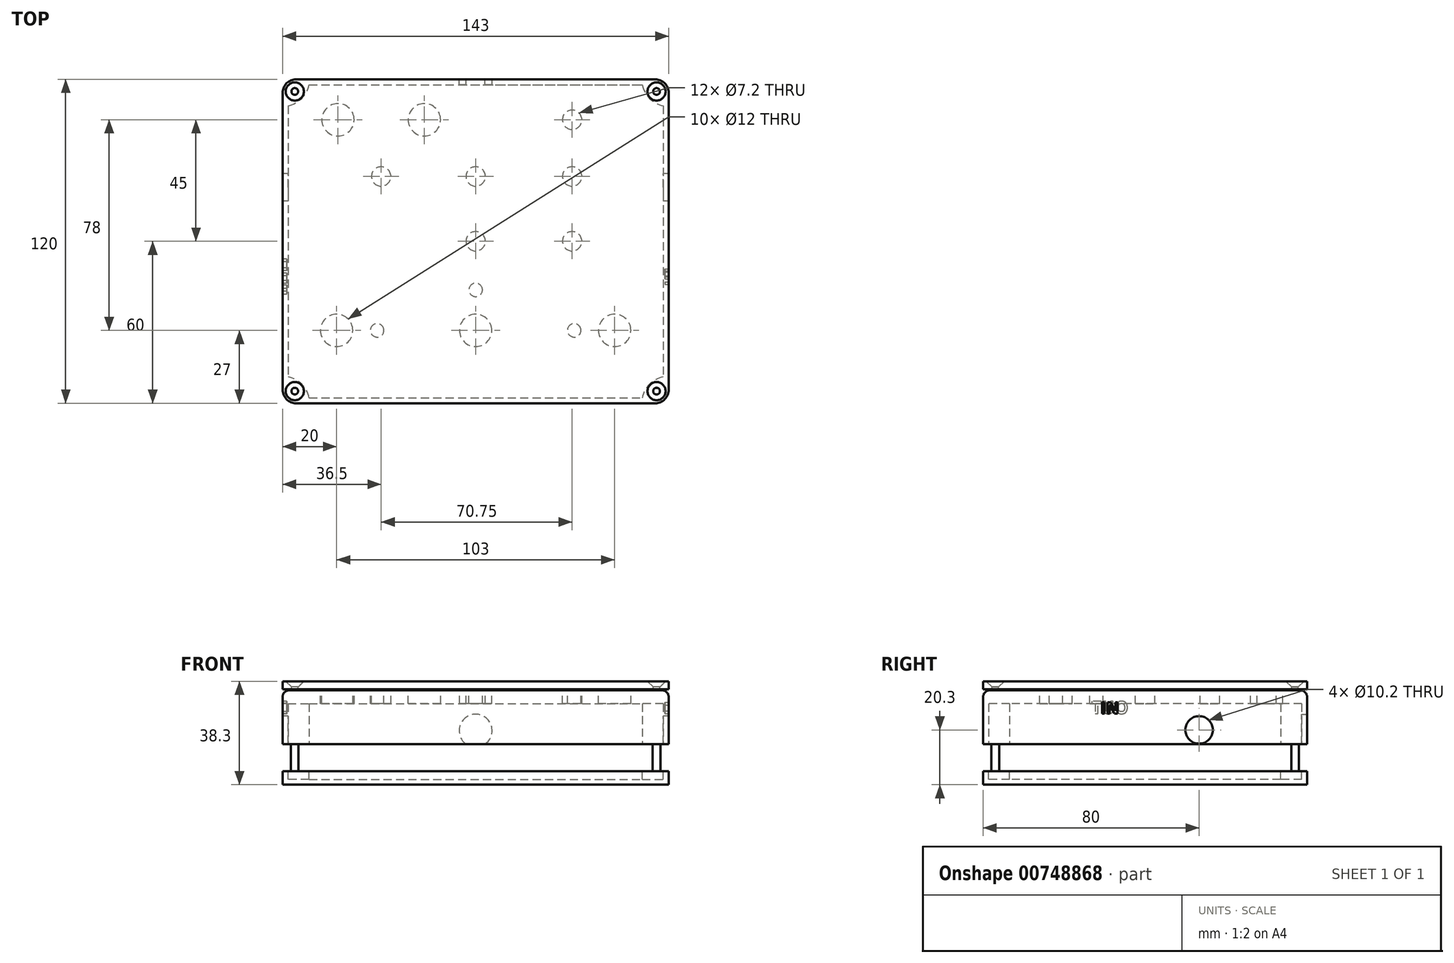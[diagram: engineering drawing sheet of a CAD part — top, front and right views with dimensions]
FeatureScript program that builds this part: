
annotation { "Feature Type Name" : "Feature", "Feature Type Description" : "" }
export const myFeature = defineFeature(function(context is Context, id is Id, definition is map)
    precondition{}
    {
        {
            var Q0;
            Q0=qCreatedBy(makeId("Top.planeOp"),FACE);
            var sketch = newSketch(context, id + "F0", { "sketchPlane" : qUnion([Q0])});
            skCircle(sketch, "E0", {"center": v(-51, 45) * mm, "radius": 6 * mm});
            skCircle(sketch, "E1", {"center": v(-19, 45) * mm, "radius": 6 * mm});
            skCircle(sketch, "E2", {"center": v(-35, 24) * mm, "radius": 3.6 * mm});
            skLineSegment(sketch, "E3", {"start": v(-51, 45) * mm, "end": v(-19, 45) * mm, "construction": true});
            skPoint(sketch, "E4.orphan", {"position": v(-57.53, 45) * mm});
            skLineSegment(sketch, "E5", {"start": v(-35, 15.96) * mm, "end": v(-35, -9.02) * mm, "construction": true});
            skPoint(sketch, "E5.startSnap0", {"position": v(-35, 45) * mm});
            skCircle(sketch, "E6", {"center": v(-51.5, -33) * mm, "radius": 6 * mm});
            skCircle(sketch, "E7", {"center": v(51.5, -33) * mm, "radius": 6 * mm});
            skLineSegment(sketch, "E8.bottom", {"start": v(-71.5, 60) * mm, "end": v(71.5, 60) * mm});
            skLineSegment(sketch, "E8.top", {"start": v(-71.5, -60) * mm, "end": v(71.5, -60) * mm});
            skLineSegment(sketch, "E8.left", {"start": v(-71.5, 60) * mm, "end": v(-71.5, -60) * mm});
            skLineSegment(sketch, "E8.right", {"start": v(71.5, 60) * mm, "end": v(71.5, -60) * mm});
            skPoint(sketch, "E9.center.orphan", {"position": v(0, -43) * mm});
            skCircle(sketch, "E10", {"center": v(0, 24) * mm, "radius": 3.6 * mm});
            skCircle(sketch, "E11", {"center": v(0, 0) * mm, "radius": 3.6 * mm});
            skCircle(sketch, "E12", {"center": v(0, -33) * mm, "radius": 6 * mm});
            skCircle(sketch, "E13", {"center": v(-36.5, -33) * mm, "radius": 2.5 * mm});
            skCircle(sketch, "E14", {"center": v(0, -18) * mm, "radius": 2.5 * mm});
            skCircle(sketch, "E15", {"center": v(36.5, -33) * mm, "radius": 2.5 * mm});
            skLineSegment(sketch, "E16", {"start": v(35.75, 70.32) * mm, "end": v(35.75, 16.59) * mm, "construction": true});
            skCircle(sketch, "E17", {"center": v(35.75, 45) * mm, "radius": 3.6 * mm});
            skCircle(sketch, "E18", {"center": v(35.75, 24) * mm, "radius": 3.6 * mm});
            skCircle(sketch, "E19", {"center": v(35.75, 0) * mm, "radius": 3.6 * mm});
            skSolve(sketch);
        }
        {
            var Q0;
            Q0=makeQuery(id+"F0.imprint","IMPRINT",FACE,{"disambiguationData":[TD([[makeQuery(id+"F0.imprint","IMPRINT",EDGE,{"derivedFrom":sQuery(id+"F0.wireOp",EDGE,"E0")}),-1.0]])]});
            extrude(context, id + "F1", {"entities" : qUnion([Q0]), "oppositeDirection" : true, "depth" : 30 * mm, "offsetDistance" : 25 * mm});
        }
        {
            var Q0;
            Q0=makeQuery(id+"F1.opExtrude","CAP_FACE",FACE,{"disambiguationData":[OSD([sQuery(id+"F0.wireOp",EDGE,"E0"),sQuery(id+"F0.wireOp",EDGE,"E1"),sQuery(id+"F0.wireOp",EDGE,"E2"),sQuery(id+"F0.wireOp",EDGE,"3e3c0a9c-ae2d-423b-a328-97259b55ec5d"),sQuery(id+"F0.wireOp",EDGE,"8074d70b-284f-45c5-9976-651f6e8f5c43"),sQuery(id+"F0.wireOp",EDGE,"4df1c9e2-d72c-4f22-b6af-1c56ed8c09ae"),sQuery(id+"F0.wireOp",EDGE,"E6"),sQuery(id+"F0.wireOp",EDGE,"E7"),sQuery(id+"F0.wireOp",EDGE,"E9"),sQuery(id+"F0.wireOp",EDGE,"E8.bottom"),sQuery(id+"F0.wireOp",EDGE,"E8.top"),sQuery(id+"F0.wireOp",EDGE,"E8.left"),sQuery(id+"F0.wireOp",EDGE,"E8.right")])],"isStart":false});
            var sketch = newSketch(context, id + "F2", { "sketchPlane" : qUnion([Q0])});
            skLineSegment(sketch, "E20.0", {"start": v(-71.5, -60) * mm, "end": v(-71.5, 60) * mm});
            skLineSegment(sketch, "E21.0", {"start": v(-71.5, 60) * mm, "end": v(71.5, 60) * mm});
            skLineSegment(sketch, "E22.0", {"start": v(71.5, -60) * mm, "end": v(71.5, 60) * mm});
            skLineSegment(sketch, "E23.0", {"start": v(-71.5, -60) * mm, "end": v(71.5, -60) * mm});
            skLineSegment(sketch, "E24.0", {"start": v(-69.5, -50.2) * mm, "end": v(-69.5, 50.2) * mm});
            skLineSegment(sketch, "E24.1", {"start": v(-61.7, -58) * mm, "end": v(61.7, -58) * mm});
            skLineSegment(sketch, "E24.2", {"start": v(69.5, -50.2) * mm, "end": v(69.5, 50.2) * mm});
            skLineSegment(sketch, "E24.3", {"start": v(-61.7, 58) * mm, "end": v(61.7, 58) * mm});
            skArc(sketch, "E25", {"start": v(-69.5, 50.2) * mm, "mid": v(-64.43, 52.93) * mm, "end": v(-61.7, 58) * mm});
            skCircle(sketch, "E26", {"center": v(-67, 55.5) * mm, "radius": 1.4 * mm});
            skArc(sketch, "E27.MirrorCS", {"start": v(69.5, 50.2) * mm, "mid": v(64.43, 52.93) * mm, "end": v(61.7, 58) * mm});
            skCircle(sketch, "E28.MirrorC", {"center": v(67, 55.5) * mm, "radius": 1.4 * mm});
            skLineSegment(sketch, "E29", {"start": v(-71.5, 0) * mm, "end": v(79.21, 0) * mm, "construction": true});
            skArc(sketch, "E30.MirrorCS", {"start": v(-69.5, -50.2) * mm, "mid": v(-64.43, -52.93) * mm, "end": v(-61.7, -58) * mm});
            skCircle(sketch, "E31.MirrorC", {"center": v(-67, -55.5) * mm, "radius": 1.4 * mm});
            skArc(sketch, "E32.MirrorCS", {"start": v(69.5, -50.2) * mm, "mid": v(64.43, -52.93) * mm, "end": v(61.7, -58) * mm});
            skCircle(sketch, "E33.MirrorC", {"center": v(67, -55.5) * mm, "radius": 1.4 * mm});
            skSolve(sketch);
        }
        {
            var Q0;
            Q0=makeQuery(id+"F2.imprint","IMPRINT",FACE,{"disambiguationData":[TD([[makeQuery(id+"F2.imprint","IMPRINT",EDGE,{"derivedFrom":sQuery(id+"F2.wireOp",EDGE,"E24.0")}),-1.0]])]});
            extrude(context, id + "F3", {"entities" : qUnion([Q0]), "operationType" : NewBodyOperationType.REMOVE, "oppositeDirection" : true, "depth" : 25 * mm, "offsetDistance" : 25 * mm});
        }
        {
            var Q0;
            Q0=makeQuery(id+"F2.imprint","IMPRINT",FACE,{"disambiguationData":[TD([[makeQuery(id+"F2.imprint","IMPRINT",EDGE,{"derivedFrom":sQuery(id+"F2.wireOp",EDGE,"E31.MirrorC")}),-1.0]])]});
            var Q1;
            Q1=makeQuery(id+"F2.imprint","IMPRINT",FACE,{"disambiguationData":[TD([[makeQuery(id+"F2.imprint","IMPRINT",EDGE,{"derivedFrom":sQuery(id+"F2.wireOp",EDGE,"E26")}),1.0]])]});
            var Q2;
            Q2=makeQuery(id+"F2.imprint","IMPRINT",FACE,{"disambiguationData":[TD([[makeQuery(id+"F2.imprint","IMPRINT",EDGE,{"derivedFrom":sQuery(id+"F2.wireOp",EDGE,"E28.MirrorC")}),-1.0]])]});
            var Q3;
            Q3=makeQuery(id+"F2.imprint","IMPRINT",FACE,{"disambiguationData":[TD([[makeQuery(id+"F2.imprint","IMPRINT",EDGE,{"derivedFrom":sQuery(id+"F2.wireOp",EDGE,"E33.MirrorC")}),1.0]])]});
            extrude(context, id + "F4", {"entities" : qUnion([Q0, Q1, Q2, Q3]), "operationType" : NewBodyOperationType.REMOVE, "oppositeDirection" : true, "depth" : 10 * mm, "offsetDistance" : 25 * mm});
        }
        {
            var Q0;
            Q0=makeQuery(id+"F1.opExtrude","SWEPT_FACE",FACE,{"disambiguationData":[OSD([sQuery(id+"F0.wireOp",EDGE,"E8.top")])]});
            var sketch = newSketch(context, id + "F5", { "sketchPlane" : qUnion([Q0])});
            skLineSegment(sketch, "E34", {"start": v(-71.5, 0.3) * mm, "end": v(-71.5, 3.3) * mm});
            skLineSegment(sketch, "E35", {"start": v(-71.5, 3.3) * mm, "end": v(71.5, 3.3) * mm});
            skLineSegment(sketch, "E36", {"start": v(71.5, 3.3) * mm, "end": v(71.5, 0.3) * mm});
            skLineSegment(sketch, "E37", {"start": v(71.5, 0.3) * mm, "end": v(-71.5, 0.3) * mm});
            skSolve(sketch);
        }
        {
            var Q0;
            Q0 = qSketchRegion(id + "F5", true);
            var Q1;
            Q1=sQuery(id+"F0.wireOp",VERTEX,"E8.left.start");
            extrude(context, id + "F6", {"entities" : qUnion([Q0]), "endBound" : BoundingType.UP_TO_VERTEX, "oppositeDirection" : true, "depth" : 100.2 * mm, "endBoundEntityVertex" : qUnion([Q1]), "offsetDistance" : 25 * mm});
        }
        {
            var Q0;
            Q0=makeQuery(id+"F1.opExtrude","SWEPT_EDGE",EDGE,{"disambiguationData":[OSD([sQuery(id+"F0.wireOp",EDGE,"E8.top"),sQuery(id+"F0.wireOp",EDGE,"E8.left")])]});
            var Q1;
            Q1=makeQuery(id+"F1.opExtrude","SWEPT_EDGE",EDGE,{"disambiguationData":[OSD([sQuery(id+"F0.wireOp",EDGE,"E8.top"),sQuery(id+"F0.wireOp",EDGE,"E8.right")])]});
            var Q2;
            Q2=makeQuery(id+"F1.opExtrude","SWEPT_EDGE",EDGE,{"disambiguationData":[OSD([sQuery(id+"F0.wireOp",EDGE,"E8.bottom"),sQuery(id+"F0.wireOp",EDGE,"E8.right")])]});
            var Q3;
            Q3=makeQuery(id+"F1.opExtrude","SWEPT_EDGE",EDGE,{"disambiguationData":[OSD([sQuery(id+"F0.wireOp",EDGE,"E8.bottom"),sQuery(id+"F0.wireOp",EDGE,"E8.left")])]});
            var Q4;
            Q4=makeQuery(id+"F6.opExtrude","CAP_EDGE",EDGE,{"disambiguationData":[OSD([sQuery(id+"F5.wireOp",EDGE,"E34")])],"isStart":true});
            var Q5;
            Q5=makeQuery(id+"F6.opExtrude","CAP_EDGE",EDGE,{"disambiguationData":[OSD([sQuery(id+"F5.wireOp",EDGE,"E36")])],"isStart":true});
            var Q6;
            Q6=makeQuery(id+"F6.opExtrude","CAP_EDGE",EDGE,{"disambiguationData":[OSD([sQuery(id+"F5.wireOp",EDGE,"E36")])],"isStart":false});
            var Q7;
            Q7=makeQuery(id+"F6.opExtrude","CAP_EDGE",EDGE,{"disambiguationData":[OSD([sQuery(id+"F5.wireOp",EDGE,"E34")])],"isStart":false});
            fillet(context, id + "F7", {"entities" : qUnion([Q0, Q1, Q2, Q3, Q4, Q5, Q6, Q7]), "radius" : 5 * mm, "tangentPropagation" : true, "allowEdgeOverflow" : false});
        }
        {
            var Q0;
            Q0=makeQuery(id+"F6.opExtrude","SWEPT_FACE",FACE,{"disambiguationData":[OSD([sQuery(id+"F5.wireOp",EDGE,"E35")])]});
            var sketch = newSketch(context, id + "F8", { "sketchPlane" : qUnion([Q0])});
            skCircle(sketch, "E38.0", {"center": v(-67, 55.5) * mm, "radius": 1.4 * mm, "construction": true});
            skCircle(sketch, "E39.1", {"center": v(-67, -55.5) * mm, "radius": 1.4 * mm, "construction": true});
            skCircle(sketch, "E40.1", {"center": v(67, -55.5) * mm, "radius": 1.4 * mm, "construction": true});
            skCircle(sketch, "E41.1", {"center": v(67, 55.5) * mm, "radius": 1.4 * mm, "construction": true});
            skSolve(sketch);
        }
        {
            var Q0;
            Q0=sQuery(id+"F8.wireOp",VERTEX,"E38.0.center");
            var Q1;
            Q1=sQuery(id+"F8.wireOp",VERTEX,"E41.1.center");
            var Q2;
            Q2=sQuery(id+"F8.wireOp",VERTEX,"E40.1.center");
            var Q3;
            Q3=sQuery(id+"F8.wireOp",VERTEX,"E39.1.center");
            var Q4;
            Q4=makeQuery(id+"F6.opExtrude","SWEPT_BODY",BODY,{"disambiguationData":[OSD([sQuery(id+"F5.wireOp",EDGE,"E34"),sQuery(id+"F5.wireOp",EDGE,"E35"),sQuery(id+"F5.wireOp",EDGE,"E36"),sQuery(id+"F5.wireOp",EDGE,"E37")])]});
            hole(context, id + "F9", {"style" : HoleStyle.C_SINK, "endStyle" : HoleEndStyle.BLIND, "standardTappedOrClearance" : lookupTablePath({ "standard" : "ISO", "engagement" : "75%", "pitch" : "0.5 mm", "size" : "M3", "type" : "Tapped" }), "standardBlindInLast" : lookupTablePath({ "standard" : "ISO", "engagement" : "75%", "pitch" : "0.5 mm", "size" : "M3", "type" : "Tapped" }), "holeDiameter" : 2.5 * mm, "cSinkDiameter" : 6.72 * mm, "cSinkAngle" : 90 * degree, "majorDiameter" : 3 * mm, "showTappedDepth" : true, "holeDepth" : 13.5 * mm, "isTappedThrough" : true, "tappedDepth" : 12 * mm, "tapClearance" : 3, "locations" : qUnion([Q0, Q1, Q2, Q3]), "scope" : qUnion([Q4])});
        }
        {
            var Q0;
            Q0=makeQuery(id+"F1.opExtrude","SWEPT_FACE",FACE,{"disambiguationData":[OSD([sQuery(id+"F0.wireOp",EDGE,"E8.left")])]});
            var sketch = newSketch(context, id + "F10", { "sketchPlane" : qUnion([Q0])});
            skCircle(sketch, "E42", {"center": v(-20, -14.7) * mm, "radius": 5.1 * mm});
            skSolve(sketch);
        }
        {
            var Q0;
            Q0 = qSketchRegion(id + "F10", true);
            extrude(context, id + "F11", {"entities" : qUnion([Q0]), "operationType" : NewBodyOperationType.REMOVE, "oppositeDirection" : true, "depth" : 158.2 * mm, "offsetDistance" : 25 * mm});
        }
        {
            var Q0;
            Q0=makeQuery(id+"F1.opExtrude","SWEPT_FACE",FACE,{"disambiguationData":[OSD([sQuery(id+"F0.wireOp",EDGE,"E8.bottom")])]});
            var sketch = newSketch(context, id + "F12", { "sketchPlane" : qUnion([Q0])});
            skCircle(sketch, "E43", {"center": v(0, -15) * mm, "radius": 6.1 * mm});
            skSolve(sketch);
        }
        {
            var Q0;
            Q0 = qSketchRegion(id + "F12", true);
            extrude(context, id + "F13", {"entities" : qUnion([Q0]), "operationType" : NewBodyOperationType.REMOVE, "oppositeDirection" : true, "depth" : 25 * mm, "offsetDistance" : 25 * mm});
        }
        {
            var Q0;
            Q0=makeQuery(id+"F1.opExtrude","SWEPT_FACE",FACE,{"disambiguationData":[OSD([sQuery(id+"F0.wireOp",EDGE,"E8.right")])]});
            var sketch = newSketch(context, id + "F14", { "sketchPlane" : qUnion([Q0])});
            skText(sketch, "E44", { "text": "IN", "fontName": "OpenSans-Bold.ttf"});
            skCircle(sketch, "E45.0", {"center": v(20, -14.7) * mm, "radius": 5.1 * mm, "construction": true});
            const initialGuessF14  = {"E44": [-0.01645, -0.0087, 1, 0, 0.00426]};
            skSetInitialGuess(sketch, initialGuessF14);
            skSolve(sketch);
        }
        {
            var Q0;
            Q0 = qSketchRegion(id + "F14", true);
            extrude(context, id + "F15", {"entities" : qUnion([Q0]), "operationType" : NewBodyOperationType.REMOVE, "oppositeDirection" : true, "depth" : 1.4 * mm, "offsetDistance" : 25 * mm});
        }
        {
            var Q0;
            Q0=makeQuery(id+"F1.opExtrude","SWEPT_FACE",FACE,{"disambiguationData":[OSD([sQuery(id+"F0.wireOp",EDGE,"E8.left")])]});
            var sketch = newSketch(context, id + "F16", { "sketchPlane" : qUnion([Q0])});
            skText(sketch, "E46", { "text": "OUT\n", "fontName": "OpenSans-Bold.ttf"});
            skCircle(sketch, "E47.0", {"center": v(-20, -14.7) * mm, "radius": 5.1 * mm, "construction": true});
            const initialGuessF16  = {"E46": [0.0062, -0.0087, 1, 0, 0.0046]};
            skSetInitialGuess(sketch, initialGuessF16);
            skSolve(sketch);
        }
        {
            var Q0;
            Q0 = qSketchRegion(id + "F16", true);
            extrude(context, id + "F17", {"entities" : qUnion([Q0]), "operationType" : NewBodyOperationType.REMOVE, "oppositeDirection" : true, "depth" : 1.5 * mm, "offsetDistance" : 25 * mm});
        }
        {
            var Q0;
            Q0=makeQuery(id+"F1.opExtrude","CAP_EDGE",EDGE,{"disambiguationData":[OSD([sQuery(id+"F0.wireOp",EDGE,"E8.top")])],"isStart":true});
            fillet(context, id + "F18", {"entities" : qUnion([Q0]), "radius" : 2.5 * mm, "tangentPropagation" : true, "allowEdgeOverflow" : false});
        }
        {
            var Q0;
            Q0=makeQuery(id+"F1.opExtrude","CAP_FACE",FACE,{"disambiguationData":[OSD([sQuery(id+"F0.wireOp",EDGE,"E0"),sQuery(id+"F0.wireOp",EDGE,"E1"),sQuery(id+"F0.wireOp",EDGE,"E2"),sQuery(id+"F0.wireOp",EDGE,"3e3c0a9c-ae2d-423b-a328-97259b55ec5d"),sQuery(id+"F0.wireOp",EDGE,"8074d70b-284f-45c5-9976-651f6e8f5c43"),sQuery(id+"F0.wireOp",EDGE,"4df1c9e2-d72c-4f22-b6af-1c56ed8c09ae"),sQuery(id+"F0.wireOp",EDGE,"E6"),sQuery(id+"F0.wireOp",EDGE,"E7"),sQuery(id+"F0.wireOp",EDGE,"E9"),sQuery(id+"F0.wireOp",EDGE,"E8.bottom"),sQuery(id+"F0.wireOp",EDGE,"E8.top"),sQuery(id+"F0.wireOp",EDGE,"E8.left"),sQuery(id+"F0.wireOp",EDGE,"E8.right")])],"isStart":true});
            var sketch = newSketch(context, id + "F19", { "sketchPlane" : qUnion([Q0])});
            skLineSegment(sketch, "E48.0", {"start": v(-69, 18.51) * mm, "end": v(-30.01, 57.5) * mm});
            skLineSegment(sketch, "E49.0", {"start": v(-69, -2.7) * mm, "end": v(-8.8, 57.5) * mm});
            skLineSegment(sketch, "E50.0", {"start": v(-69, -23.91) * mm, "end": v(12.41, 57.5) * mm});
            skLineSegment(sketch, "E51.0", {"start": v(-69, -45.12) * mm, "end": v(33.62, 57.5) * mm});
            skLineSegment(sketch, "E52.0", {"start": v(-62.66, -60) * mm, "end": v(54.84, 57.5) * mm});
            skLineSegment(sketch, "E53.0", {"start": v(-41.45, -60) * mm, "end": v(69, 50.45) * mm});
            skLineSegment(sketch, "E54.0", {"start": v(-20.24, -60) * mm, "end": v(69, 29.24) * mm});
            skLineSegment(sketch, "E55.0", {"start": v(0.98, -60) * mm, "end": v(69, 8.02) * mm});
            skLineSegment(sketch, "E56.0", {"start": v(22.2, -60) * mm, "end": v(69, -13.2) * mm});
            skLineSegment(sketch, "E57.0", {"start": v(43.4, -60) * mm, "end": v(69, -34.4) * mm});
            skLineSegment(sketch, "E58.0", {"start": v(-69, 39.73) * mm, "end": v(-51.23, 57.5) * mm});
            skLineSegment(sketch, "E59", {"start": v(-68.27, 56.77) * mm, "end": v(68.27, -56.77) * mm});
            skSolve(sketch);
        }
        {
            var Q0;
            Q0=makeQuery(id+"F1.opExtrude","CAP_FACE",FACE,{"disambiguationData":[OSD([sQuery(id+"F0.wireOp",EDGE,"E0"),sQuery(id+"F0.wireOp",EDGE,"E1"),sQuery(id+"F0.wireOp",EDGE,"E2"),sQuery(id+"F0.wireOp",EDGE,"3e3c0a9c-ae2d-423b-a328-97259b55ec5d"),sQuery(id+"F0.wireOp",EDGE,"8074d70b-284f-45c5-9976-651f6e8f5c43"),sQuery(id+"F0.wireOp",EDGE,"4df1c9e2-d72c-4f22-b6af-1c56ed8c09ae"),sQuery(id+"F0.wireOp",EDGE,"E6"),sQuery(id+"F0.wireOp",EDGE,"E7"),sQuery(id+"F0.wireOp",EDGE,"E9"),sQuery(id+"F0.wireOp",EDGE,"E8.bottom"),sQuery(id+"F0.wireOp",EDGE,"E8.top"),sQuery(id+"F0.wireOp",EDGE,"E8.left"),sQuery(id+"F0.wireOp",EDGE,"E8.right")])],"isStart":false});
            var sketch = newSketch(context, id + "F20", { "sketchPlane" : qUnion([Q0])});
            skLineSegment(sketch, "E60.0", {"start": v(-71.5, -55) * mm, "end": v(-71.5, 55) * mm});
            skArc(sketch, "E60.1", {"start": v(-66.5, 60) * mm, "mid": v(-70.04, 58.54) * mm, "end": v(-71.5, 55) * mm});
            skLineSegment(sketch, "E60.2", {"start": v(-66.5, 60) * mm, "end": v(66.5, 60) * mm});
            skArc(sketch, "E60.3", {"start": v(71.5, 55) * mm, "mid": v(70.04, 58.54) * mm, "end": v(66.5, 60) * mm});
            skLineSegment(sketch, "E60.4", {"start": v(71.5, -55) * mm, "end": v(71.5, 55) * mm});
            skArc(sketch, "E60.5", {"start": v(66.5, -60) * mm, "mid": v(70.04, -58.54) * mm, "end": v(71.5, -55) * mm});
            skLineSegment(sketch, "E60.6", {"start": v(-66.5, -60) * mm, "end": v(66.5, -60) * mm});
            skArc(sketch, "E60.7", {"start": v(-71.5, -55) * mm, "mid": v(-70.04, -58.54) * mm, "end": v(-66.5, -60) * mm});
            skLineSegment(sketch, "E61.0", {"start": v(-69.5, -50.2) * mm, "end": v(-69.5, 50.2) * mm});
            skArc(sketch, "E61.1", {"start": v(-69.5, 50.2) * mm, "mid": v(-64.43, 52.93) * mm, "end": v(-61.7, 58) * mm});
            skLineSegment(sketch, "E61.2", {"start": v(-61.7, 58) * mm, "end": v(61.7, 58) * mm});
            skArc(sketch, "E61.3", {"start": v(69.5, 50.2) * mm, "mid": v(64.43, 52.93) * mm, "end": v(61.7, 58) * mm});
            skLineSegment(sketch, "E61.4", {"start": v(69.5, -50.2) * mm, "end": v(69.5, 50.2) * mm});
            skArc(sketch, "E61.5", {"start": v(69.5, -50.2) * mm, "mid": v(64.43, -52.93) * mm, "end": v(61.7, -58) * mm});
            skLineSegment(sketch, "E61.6", {"start": v(-61.7, -58) * mm, "end": v(61.7, -58) * mm});
            skArc(sketch, "E61.7", {"start": v(-69.5, -50.2) * mm, "mid": v(-64.43, -52.93) * mm, "end": v(-61.7, -58) * mm});
            skSolve(sketch);
        }
        {
            var Q0;
            Q0 = qSketchRegion(id + "F20", true);
            extrude(context, id + "F21", {"entities" : qUnion([Q0]), "depth" : 3 * mm, "offsetDistance" : 25 * mm});
        }
        {
            var Q0;
            Q0=makeQuery(id+"F21.opExtrude","CAP_FACE",FACE,{"disambiguationData":[OSD([sQuery(id+"F20.wireOp",EDGE,"E60.0"),sQuery(id+"F20.wireOp",EDGE,"E60.1"),sQuery(id+"F20.wireOp",EDGE,"E60.2"),sQuery(id+"F20.wireOp",EDGE,"E60.3"),sQuery(id+"F20.wireOp",EDGE,"E60.4"),sQuery(id+"F20.wireOp",EDGE,"E60.5"),sQuery(id+"F20.wireOp",EDGE,"E60.6"),sQuery(id+"F20.wireOp",EDGE,"E60.7"),sQuery(id+"F20.wireOp",EDGE,"E61.0"),sQuery(id+"F20.wireOp",EDGE,"E61.1"),sQuery(id+"F20.wireOp",EDGE,"E61.2"),sQuery(id+"F20.wireOp",EDGE,"E61.3"),sQuery(id+"F20.wireOp",EDGE,"E61.4"),sQuery(id+"F20.wireOp",EDGE,"E61.5"),sQuery(id+"F20.wireOp",EDGE,"E61.6"),sQuery(id+"F20.wireOp",EDGE,"E61.7")])],"isStart":false});
            var sketch = newSketch(context, id + "F22", { "sketchPlane" : qUnion([Q0])});
            skLineSegment(sketch, "E62.0", {"start": v(-71.5, -55) * mm, "end": v(-71.5, 55) * mm});
            skArc(sketch, "E62.1", {"start": v(-66.5, 60) * mm, "mid": v(-70.04, 58.54) * mm, "end": v(-71.5, 55) * mm});
            skLineSegment(sketch, "E62.2", {"start": v(-66.5, 60) * mm, "end": v(66.5, 60) * mm});
            skArc(sketch, "E62.3", {"start": v(71.5, 55) * mm, "mid": v(70.04, 58.54) * mm, "end": v(66.5, 60) * mm});
            skLineSegment(sketch, "E62.4", {"start": v(71.5, -55) * mm, "end": v(71.5, 55) * mm});
            skArc(sketch, "E62.5", {"start": v(66.5, -60) * mm, "mid": v(70.04, -58.54) * mm, "end": v(71.5, -55) * mm});
            skLineSegment(sketch, "E62.6", {"start": v(-66.5, -60) * mm, "end": v(66.5, -60) * mm});
            skArc(sketch, "E62.7", {"start": v(-71.5, -55) * mm, "mid": v(-70.04, -58.54) * mm, "end": v(-66.5, -60) * mm});
            skSolve(sketch);
        }
        {
            var Q0;
            Q0 = qSketchRegion(id + "F22", true);
            extrude(context, id + "F23", {"entities" : qUnion([Q0]), "operationType" : NewBodyOperationType.ADD, "depth" : 2 * mm, "offsetDistance" : 25 * mm});
        }
    });
